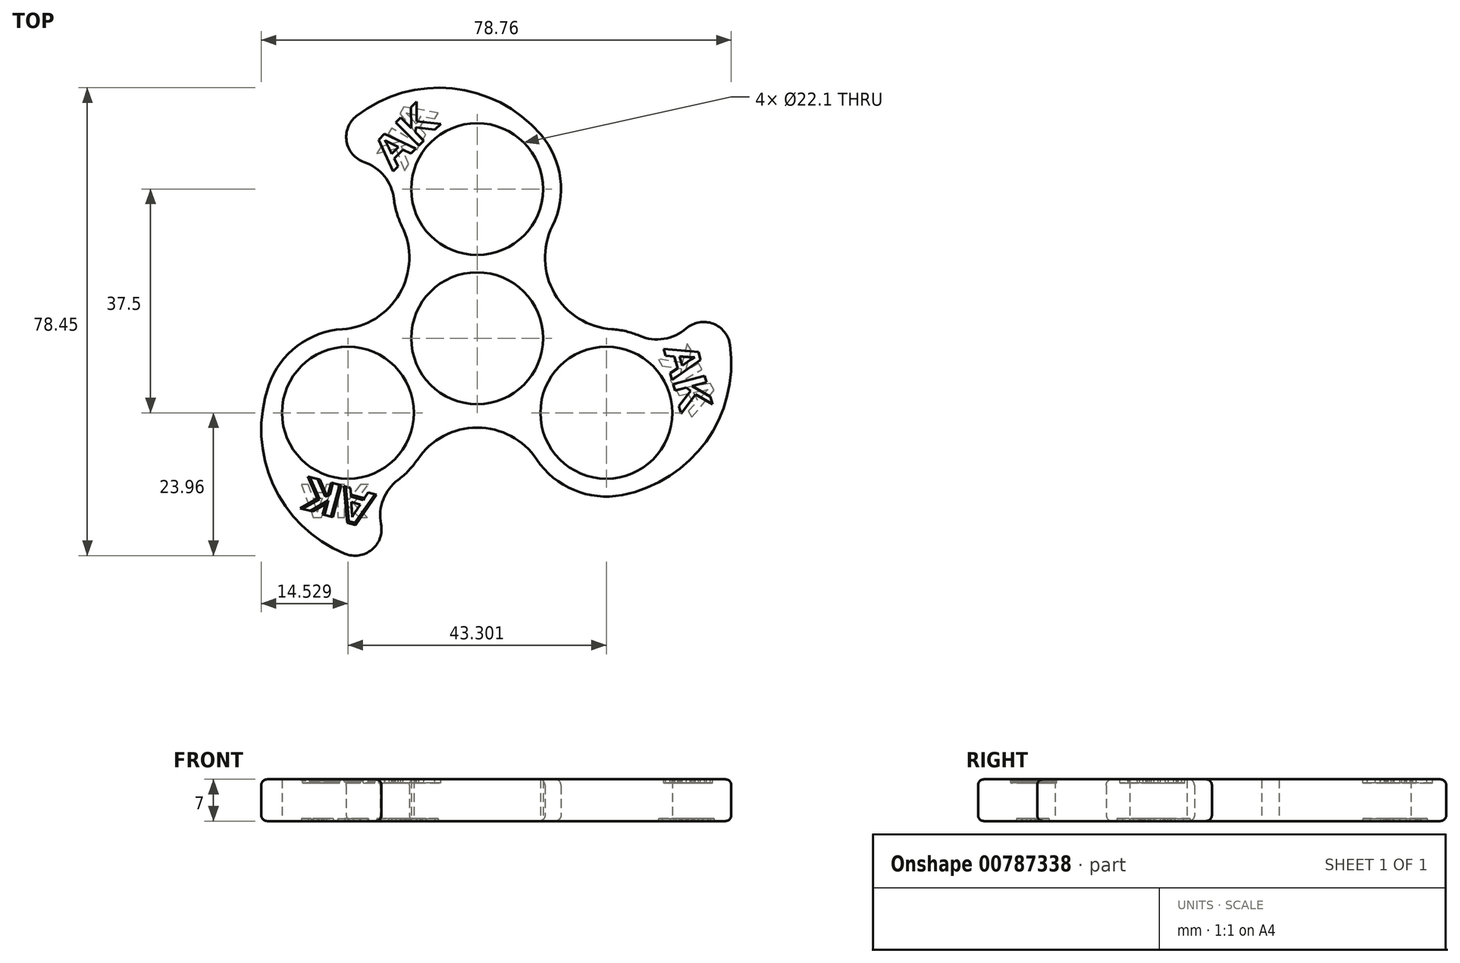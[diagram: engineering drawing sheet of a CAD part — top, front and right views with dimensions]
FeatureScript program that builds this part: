
annotation { "Feature Type Name" : "Feature", "Feature Type Description" : "" }
export const myFeature = defineFeature(function(context is Context, id is Id, definition is map)
    precondition{}
    {
        {
            var Q0;
            Q0=qCreatedBy(makeId("Top.planeOp"),FACE);
            var sketch = newSketch(context, id + "F0", { "sketchPlane" : qUnion([Q0])});
            skCircle(sketch, "E0", {"center": v(0, 0) * mm, "radius": 11.05 * mm});
            skCircle(sketch, "E1", {"center": v(0, 0) * mm, "radius": 16.5 * mm});
            skCircle(sketch, "E2", {"center": v(0, 25) * mm, "radius": 11.05 * mm});
            skCircle(sketch, "E3", {"center": v(0, 25) * mm, "radius": 14.05 * mm});
            skLineSegment(sketch, "E4", {"start": v(0, 0) * mm, "end": v(-33.5, -19.34) * mm, "construction": true});
            skLineSegment(sketch, "E5", {"start": v(35.5, -20.5) * mm, "end": v(0, 0) * mm, "construction": true});
            skLineSegment(sketch, "E6", {"start": v(0, 0) * mm, "end": v(54.09, 31.23) * mm, "construction": true});
            skCircle(sketch, "E7", {"center": v(23.37, 13.5) * mm, "radius": 12 * mm});
            skCircle(sketch, "E8", {"center": v(0, 0) * mm, "radius": 38 * mm});
            skCircle(sketch, "E9.1.0", {"center": v(-23.37, 13.5) * mm, "radius": 12 * mm});
            skCircle(sketch, "E9.2.0", {"center": v(0, -26.99) * mm, "radius": 12 * mm});
            skCircle(sketch, "E10.1.0", {"center": v(-21.65, -12.5) * mm, "radius": 14.05 * mm});
            skCircle(sketch, "E10.1.1", {"center": v(-21.65, -12.5) * mm, "radius": 11.05 * mm});
            skCircle(sketch, "E10.2.0", {"center": v(21.65, -12.5) * mm, "radius": 14.05 * mm});
            skCircle(sketch, "E10.2.1", {"center": v(21.65, -12.5) * mm, "radius": 11.05 * mm});
            skCircle(sketch, "E11", {"center": v(-17.48, 33.74) * mm, "radius": 4.46 * mm});
            skCircle(sketch, "E12", {"center": v(-21.34, 22.5) * mm, "radius": 7.43 * mm});
            skCircle(sketch, "E13", {"center": v(-6.4, 19.5) * mm, "radius": 22.5 * mm});
            skCircle(sketch, "E14.1.0", {"center": v(-20.48, -32) * mm, "radius": 4.46 * mm});
            skCircle(sketch, "E14.1.1", {"center": v(-13.68, -15.3) * mm, "radius": 22.5 * mm});
            skCircle(sketch, "E14.1.2", {"center": v(-8.82, -29.73) * mm, "radius": 7.43 * mm});
            skCircle(sketch, "E14.2.0", {"center": v(37.96, -1.73) * mm, "radius": 4.46 * mm});
            skCircle(sketch, "E14.2.1", {"center": v(20.08, -4.2) * mm, "radius": 22.5 * mm});
            skCircle(sketch, "E14.2.2", {"center": v(30.15, 7.23) * mm, "radius": 7.43 * mm});
            skSolve(sketch);
        }
        {
            var Q0;
            {var subQ0=sQuery(id+"F0.wireOp",EDGE,"E8");var subQ1=sQuery(id+"F0.wireOp",EDGE,"E3");var subQ2=makeQuery(id+"F0.imprint","INTERSECT",VERTEX,{"disambiguationData":[OD(0.0)],"derivedFrom":[subQ1,subQ0]});Q0=makeQuery(id+"F0.imprint","IMPRINT",FACE,{"disambiguationData":[TD([[makeQuery(id+"F0.imprint","IMPRINT",EDGE,{"disambiguationData":[TD([[subQ2,-1.0]])],"derivedFrom":subQ1}),1.0]])]});}
            var Q1;
            {var subQ1=sQuery(id+"F0.wireOp",EDGE,"E3");var subQ6=sQuery(id+"F0.wireOp",EDGE,"E1");var subQ11=makeQuery(id+"F0.imprint","INTERSECT",VERTEX,{"disambiguationData":[OD(0.0)],"derivedFrom":[subQ6,subQ1]});Q1=makeQuery(id+"F0.imprint","IMPRINT",FACE,{"disambiguationData":[TD([[makeQuery(id+"F0.imprint","IMPRINT",EDGE,{"disambiguationData":[TD([[subQ11,-1.0]])],"derivedFrom":subQ6}),-1.0]])]});}
            var Q2;
            {var subQ0=sQuery(id+"F0.wireOp",EDGE,"E9.1.0");var subQ1=sQuery(id+"F0.wireOp",EDGE,"E3");var subQ2=makeQuery(id+"F0.imprint","INTERSECT",VERTEX,{"disambiguationData":[OD(0.0)],"derivedFrom":[subQ1,subQ0]});Q2=makeQuery(id+"F0.imprint","IMPRINT",FACE,{"disambiguationData":[TD([[makeQuery(id+"F0.imprint","IMPRINT",EDGE,{"disambiguationData":[TD([[subQ2,-1.0]])],"derivedFrom":subQ1}),1.0]])]});}
            var Q3;
            {var subQ0=sQuery(id+"F0.wireOp",EDGE,"E7");var subQ1=sQuery(id+"F0.wireOp",EDGE,"E3");var subQ2=makeQuery(id+"F0.imprint","INTERSECT",VERTEX,{"disambiguationData":[OD(0.0)],"derivedFrom":[subQ1,subQ0]});Q3=makeQuery(id+"F0.imprint","IMPRINT",FACE,{"disambiguationData":[TD([[makeQuery(id+"F0.imprint","IMPRINT",EDGE,{"disambiguationData":[TD([[subQ2,1.0]])],"derivedFrom":subQ1}),1.0]])]});}
            var Q4;
            {var subQ4=sQuery(id+"F0.wireOp",EDGE,"E3");var subQ7=sQuery(id+"F0.wireOp",EDGE,"E0");var subQ8=makeQuery(id+"F0.imprint","INTERSECT",VERTEX,{"disambiguationData":[OD(0.0)],"derivedFrom":[subQ7,subQ4]});Q4=makeQuery(id+"F0.imprint","IMPRINT",FACE,{"disambiguationData":[TD([[makeQuery(id+"F0.imprint","IMPRINT",EDGE,{"disambiguationData":[TD([[subQ8,-1.0]])],"derivedFrom":subQ7}),-1.0]])]});}
            var Q5;
            {var subQ0=sQuery(id+"F0.wireOp",EDGE,"E3");var subQ1=sQuery(id+"F0.wireOp",EDGE,"E0");var subQ2=makeQuery(id+"F0.imprint","INTERSECT",VERTEX,{"disambiguationData":[OD(1.0)],"derivedFrom":[subQ1,subQ0]});Q5=makeQuery(id+"F0.imprint","IMPRINT",FACE,{"disambiguationData":[TD([[makeQuery(id+"F0.imprint","IMPRINT",EDGE,{"disambiguationData":[TD([[subQ2,-1.0]])],"derivedFrom":subQ1}),-1.0]])]});}
            var Q6;
            {var subQ0=sQuery(id+"F0.wireOp",EDGE,"E3");var subQ1=sQuery(id+"F0.wireOp",EDGE,"E0");var subQ2=makeQuery(id+"F0.imprint","INTERSECT",VERTEX,{"disambiguationData":[OD(0.0)],"derivedFrom":[subQ1,subQ0]});Q6=makeQuery(id+"F0.imprint","IMPRINT",FACE,{"disambiguationData":[TD([[makeQuery(id+"F0.imprint","IMPRINT",EDGE,{"disambiguationData":[TD([[subQ2,1.0]])],"derivedFrom":subQ1}),-1.0]])]});}
            var Q7;
            {var subQ0=sQuery(id+"F0.wireOp",EDGE,"E10.2.0");var subQ1=sQuery(id+"F0.wireOp",EDGE,"E0");var subQ2=makeQuery(id+"F0.imprint","INTERSECT",VERTEX,{"disambiguationData":[OD(0.0)],"derivedFrom":[subQ1,subQ0]});Q7=makeQuery(id+"F0.imprint","IMPRINT",FACE,{"disambiguationData":[TD([[makeQuery(id+"F0.imprint","IMPRINT",EDGE,{"disambiguationData":[TD([[subQ2,1.0]])],"derivedFrom":subQ1}),-1.0]])]});}
            var Q8;
            {var subQ0=sQuery(id+"F0.wireOp",EDGE,"E10.1.0");var subQ1=sQuery(id+"F0.wireOp",EDGE,"E0");var subQ2=makeQuery(id+"F0.imprint","INTERSECT",VERTEX,{"disambiguationData":[OD(1.0)],"derivedFrom":[subQ1,subQ0]});Q8=makeQuery(id+"F0.imprint","IMPRINT",FACE,{"disambiguationData":[TD([[makeQuery(id+"F0.imprint","IMPRINT",EDGE,{"disambiguationData":[TD([[subQ2,-1.0]])],"derivedFrom":subQ1}),-1.0]])]});}
            var Q9;
            {var subQ0=sQuery(id+"F0.wireOp",EDGE,"E10.1.0");var subQ1=sQuery(id+"F0.wireOp",EDGE,"E0");var subQ9=makeQuery(id+"F0.imprint","INTERSECT",VERTEX,{"disambiguationData":[OD(0.0)],"derivedFrom":[subQ1,subQ0]});Q9=makeQuery(id+"F0.imprint","IMPRINT",FACE,{"disambiguationData":[TD([[makeQuery(id+"F0.imprint","IMPRINT",EDGE,{"disambiguationData":[TD([[subQ9,-1.0]])],"derivedFrom":subQ1}),-1.0]])]});}
            var Q10;
            {var subQ0=sQuery(id+"F0.wireOp",EDGE,"E10.1.0");var subQ7=sQuery(id+"F0.wireOp",EDGE,"E1");var subQ14=makeQuery(id+"F0.imprint","INTERSECT",VERTEX,{"disambiguationData":[OD(0.0)],"derivedFrom":[subQ7,subQ0]});Q10=makeQuery(id+"F0.imprint","IMPRINT",FACE,{"disambiguationData":[TD([[makeQuery(id+"F0.imprint","IMPRINT",EDGE,{"disambiguationData":[TD([[subQ14,-1.0]])],"derivedFrom":subQ7}),-1.0]])]});}
            var Q11;
            {var subQ0=sQuery(id+"F0.wireOp",EDGE,"E10.1.0");var subQ1=sQuery(id+"F0.wireOp",EDGE,"E8");var subQ2=makeQuery(id+"F0.imprint","INTERSECT",VERTEX,{"disambiguationData":[OD(0.0)],"derivedFrom":[subQ1,subQ0]});Q11=makeQuery(id+"F0.imprint","IMPRINT",FACE,{"disambiguationData":[TD([[makeQuery(id+"F0.imprint","IMPRINT",EDGE,{"disambiguationData":[TD([[subQ2,-1.0]])],"derivedFrom":subQ1}),-1.0]])]});}
            var Q12;
            {var subQ0=sQuery(id+"F0.wireOp",EDGE,"E10.2.0");var subQ7=sQuery(id+"F0.wireOp",EDGE,"E1");var subQ15=makeQuery(id+"F0.imprint","INTERSECT",VERTEX,{"disambiguationData":[OD(1.0)],"derivedFrom":[subQ7,subQ0]});Q12=makeQuery(id+"F0.imprint","IMPRINT",FACE,{"disambiguationData":[TD([[makeQuery(id+"F0.imprint","IMPRINT",EDGE,{"disambiguationData":[TD([[subQ15,-1.0]])],"derivedFrom":subQ7}),-1.0]])]});}
            var Q13;
            {var subQ0=sQuery(id+"F0.wireOp",EDGE,"E10.2.0");var subQ1=sQuery(id+"F0.wireOp",EDGE,"E8");var subQ2=makeQuery(id+"F0.imprint","INTERSECT",VERTEX,{"disambiguationData":[OD(0.0)],"derivedFrom":[subQ1,subQ0]});Q13=makeQuery(id+"F0.imprint","IMPRINT",FACE,{"disambiguationData":[TD([[makeQuery(id+"F0.imprint","IMPRINT",EDGE,{"disambiguationData":[TD([[subQ2,-1.0]])],"derivedFrom":subQ1}),-1.0]])]});}
            var Q14;
            {var subQ0=sQuery(id+"F0.wireOp",EDGE,"E3");var subQ1=sQuery(id+"F0.wireOp",EDGE,"E1");var subQ2=makeQuery(id+"F0.imprint","INTERSECT",VERTEX,{"disambiguationData":[OD(0.0)],"derivedFrom":[subQ1,subQ0]});Q14=makeQuery(id+"F0.imprint","IMPRINT",FACE,{"disambiguationData":[TD([[makeQuery(id+"F0.imprint","IMPRINT",EDGE,{"disambiguationData":[TD([[subQ2,1.0]])],"derivedFrom":subQ1}),-1.0]])]});}
            var Q15;
            {var subQ0=sQuery(id+"F0.wireOp",EDGE,"E3");var subQ1=sQuery(id+"F0.wireOp",EDGE,"E1");var subQ2=makeQuery(id+"F0.imprint","INTERSECT",VERTEX,{"disambiguationData":[OD(1.0)],"derivedFrom":[subQ1,subQ0]});Q15=makeQuery(id+"F0.imprint","IMPRINT",FACE,{"disambiguationData":[TD([[makeQuery(id+"F0.imprint","IMPRINT",EDGE,{"disambiguationData":[TD([[subQ2,-1.0]])],"derivedFrom":subQ1}),-1.0]])]});}
            var Q16;
            {var subQ0=sQuery(id+"F0.wireOp",EDGE,"E10.1.0");var subQ1=sQuery(id+"F0.wireOp",EDGE,"E1");var subQ2=makeQuery(id+"F0.imprint","INTERSECT",VERTEX,{"disambiguationData":[OD(1.0)],"derivedFrom":[subQ1,subQ0]});Q16=makeQuery(id+"F0.imprint","IMPRINT",FACE,{"disambiguationData":[TD([[makeQuery(id+"F0.imprint","IMPRINT",EDGE,{"disambiguationData":[TD([[subQ2,-1.0]])],"derivedFrom":subQ1}),-1.0]])]});}
            var Q17;
            {var subQ0=sQuery(id+"F0.wireOp",EDGE,"E8");var subQ1=sQuery(id+"F0.wireOp",EDGE,"E3");var subQ2=makeQuery(id+"F0.imprint","INTERSECT",VERTEX,{"disambiguationData":[OD(0.0)],"derivedFrom":[subQ1,subQ0]});Q17=makeQuery(id+"F0.imprint","IMPRINT",FACE,{"disambiguationData":[TD([[makeQuery(id+"F0.imprint","IMPRINT",EDGE,{"disambiguationData":[TD([[subQ2,1.0]])],"derivedFrom":subQ1}),1.0]])]});}
            var Q18;
            {var subQ0=sQuery(id+"F0.wireOp",EDGE,"E10.1.0");var subQ2=sQuery(id+"F0.wireOp",EDGE,"E1");var subQ4=makeQuery(id+"F0.imprint","INTERSECT",VERTEX,{"disambiguationData":[OD(0.0)],"derivedFrom":[subQ2,subQ0]});Q18=makeQuery(id+"F0.imprint","IMPRINT",FACE,{"disambiguationData":[TD([[makeQuery(id+"F0.imprint","IMPRINT",EDGE,{"disambiguationData":[TD([[subQ4,-1.0]])],"derivedFrom":subQ2}),1.0]])]});}
            var Q19;
            {var subQ1=sQuery(id+"F0.wireOp",EDGE,"E1");var subQ3=sQuery(id+"F0.wireOp",EDGE,"E3");var subQ7=makeQuery(id+"F0.imprint","INTERSECT",VERTEX,{"disambiguationData":[OD(0.0)],"derivedFrom":[subQ1,subQ3]});Q19=makeQuery(id+"F0.imprint","IMPRINT",FACE,{"disambiguationData":[TD([[makeQuery(id+"F0.imprint","IMPRINT",EDGE,{"disambiguationData":[TD([[subQ7,-1.0]])],"derivedFrom":subQ1}),1.0]])]});}
            var Q20;
            {var subQ0=sQuery(id+"F0.wireOp",EDGE,"E10.2.0");var subQ2=sQuery(id+"F0.wireOp",EDGE,"E1");var subQ6=makeQuery(id+"F0.imprint","INTERSECT",VERTEX,{"disambiguationData":[OD(1.0)],"derivedFrom":[subQ2,subQ0]});Q20=makeQuery(id+"F0.imprint","IMPRINT",FACE,{"disambiguationData":[TD([[makeQuery(id+"F0.imprint","IMPRINT",EDGE,{"disambiguationData":[TD([[subQ6,-1.0]])],"derivedFrom":subQ2}),1.0]])]});}
            var Q21;
            {var subQ0=sQuery(id+"F0.wireOp",EDGE,"E7");var subQ1=sQuery(id+"F0.wireOp",EDGE,"E1");var subQ2=makeQuery(id+"F0.imprint","INTERSECT",VERTEX,{"disambiguationData":[OD(0.0)],"derivedFrom":[subQ1,subQ0]});Q21=makeQuery(id+"F0.imprint","IMPRINT",FACE,{"disambiguationData":[TD([[makeQuery(id+"F0.imprint","IMPRINT",EDGE,{"disambiguationData":[TD([[subQ2,1.0]])],"derivedFrom":subQ1}),-1.0]])]});}
            var Q22;
            {var subQ0=sQuery(id+"F0.wireOp",EDGE,"E9.1.0");var subQ1=sQuery(id+"F0.wireOp",EDGE,"E1");var subQ2=makeQuery(id+"F0.imprint","INTERSECT",VERTEX,{"disambiguationData":[OD(1.0)],"derivedFrom":[subQ1,subQ0]});Q22=makeQuery(id+"F0.imprint","IMPRINT",FACE,{"disambiguationData":[TD([[makeQuery(id+"F0.imprint","IMPRINT",EDGE,{"disambiguationData":[TD([[subQ2,-1.0]])],"derivedFrom":subQ1}),-1.0]])]});}
            var Q23;
            {var subQ0=sQuery(id+"F0.wireOp",EDGE,"E9.2.0");var subQ1=sQuery(id+"F0.wireOp",EDGE,"E1");var subQ2=makeQuery(id+"F0.imprint","INTERSECT",VERTEX,{"disambiguationData":[OD(1.0)],"derivedFrom":[subQ1,subQ0]});Q23=makeQuery(id+"F0.imprint","IMPRINT",FACE,{"disambiguationData":[TD([[makeQuery(id+"F0.imprint","IMPRINT",EDGE,{"disambiguationData":[TD([[subQ2,-1.0]])],"derivedFrom":subQ1}),-1.0]])]});}
            var Q24;
            {var subQ0=sQuery(id+"F0.wireOp",EDGE,"E8");var subQ1=sQuery(id+"F0.wireOp",EDGE,"E3");var subQ2=makeQuery(id+"F0.imprint","INTERSECT",VERTEX,{"disambiguationData":[OD(1.0)],"derivedFrom":[subQ1,subQ0]});Q24=makeQuery(id+"F0.imprint","IMPRINT",FACE,{"disambiguationData":[TD([[makeQuery(id+"F0.imprint","IMPRINT",EDGE,{"disambiguationData":[TD([[subQ2,-1.0]])],"derivedFrom":subQ1}),-1.0]])]});}
            var Q25;
            {var subQ0=sQuery(id+"F0.wireOp",EDGE,"E8");var subQ1=sQuery(id+"F0.wireOp",EDGE,"E3");var subQ2=makeQuery(id+"F0.imprint","INTERSECT",VERTEX,{"disambiguationData":[OD(0.0)],"derivedFrom":[subQ1,subQ0]});Q25=makeQuery(id+"F0.imprint","IMPRINT",FACE,{"disambiguationData":[TD([[makeQuery(id+"F0.imprint","IMPRINT",EDGE,{"disambiguationData":[TD([[subQ2,-1.0]])],"derivedFrom":subQ1}),-1.0]])]});}
            var Q26;
            {var subQ0=sQuery(id+"F0.wireOp",EDGE,"E11");var subQ1=sQuery(id+"F0.wireOp",EDGE,"E8");var subQ2=makeQuery(id+"F0.imprint","INTERSECT",VERTEX,{"disambiguationData":[OD(0.0)],"derivedFrom":[subQ1,subQ0]});Q26=makeQuery(id+"F0.imprint","IMPRINT",FACE,{"disambiguationData":[TD([[makeQuery(id+"F0.imprint","IMPRINT",EDGE,{"disambiguationData":[TD([[subQ2,-1.0]])],"derivedFrom":subQ1}),1.0]])]});}
            var Q27;
            {var subQ2=sQuery(id+"F0.wireOp",EDGE,"E13");var subQ4=sQuery(id+"F0.wireOp",EDGE,"E1");var subQ5=makeQuery(id+"F0.imprint","INTERSECT",VERTEX,{"disambiguationData":[OD(1.0)],"derivedFrom":[subQ4,subQ2]});Q27=makeQuery(id+"F0.imprint","IMPRINT",FACE,{"disambiguationData":[TD([[makeQuery(id+"F0.imprint","IMPRINT",EDGE,{"disambiguationData":[TD([[subQ5,-1.0]])],"derivedFrom":subQ4}),1.0]])]});}
            var Q28;
            {var subQ0=sQuery(id+"F0.wireOp",EDGE,"E13");var subQ1=sQuery(id+"F0.wireOp",EDGE,"E0");var subQ2=makeQuery(id+"F0.imprint","INTERSECT",VERTEX,{"disambiguationData":[OD(1.0)],"derivedFrom":[subQ1,subQ0]});Q28=makeQuery(id+"F0.imprint","IMPRINT",FACE,{"disambiguationData":[TD([[makeQuery(id+"F0.imprint","IMPRINT",EDGE,{"disambiguationData":[TD([[subQ2,-1.0]])],"derivedFrom":subQ1}),-1.0]])]});}
            var Q29;
            {var subQ0=sQuery(id+"F0.wireOp",EDGE,"E11");var subQ1=sQuery(id+"F0.wireOp",EDGE,"E8");var subQ2=makeQuery(id+"F0.imprint","INTERSECT",VERTEX,{"disambiguationData":[OD(0.0)],"derivedFrom":[subQ1,subQ0]});Q29=makeQuery(id+"F0.imprint","IMPRINT",FACE,{"disambiguationData":[TD([[makeQuery(id+"F0.imprint","IMPRINT",EDGE,{"disambiguationData":[TD([[subQ2,-1.0]])],"derivedFrom":subQ1}),-1.0]])]});}
            var Q30;
            {var subQ2=sQuery(id+"F0.wireOp",EDGE,"E1");var subQ7=sQuery(id+"F0.wireOp",EDGE,"E14.2.1");var subQ8=makeQuery(id+"F0.imprint","INTERSECT",VERTEX,{"disambiguationData":[OD(0.0)],"derivedFrom":[subQ2,subQ7]});Q30=makeQuery(id+"F0.imprint","IMPRINT",FACE,{"disambiguationData":[TD([[makeQuery(id+"F0.imprint","IMPRINT",EDGE,{"disambiguationData":[TD([[subQ8,-1.0]])],"derivedFrom":subQ2}),1.0]])]});}
            var Q31;
            {var subQ7=sQuery(id+"F0.wireOp",EDGE,"E14.2.1");var subQ9=sQuery(id+"F0.wireOp",EDGE,"E0");var subQ10=makeQuery(id+"F0.imprint","INTERSECT",VERTEX,{"disambiguationData":[OD(0.0)],"derivedFrom":[subQ9,subQ7]});Q31=makeQuery(id+"F0.imprint","IMPRINT",FACE,{"disambiguationData":[TD([[makeQuery(id+"F0.imprint","IMPRINT",EDGE,{"disambiguationData":[TD([[subQ10,1.0]])],"derivedFrom":subQ9}),-1.0]])]});}
            var Q32;
            {var subQ0=sQuery(id+"F0.wireOp",EDGE,"E14.2.1");var subQ1=sQuery(id+"F0.wireOp",EDGE,"E3");var subQ2=makeQuery(id+"F0.imprint","INTERSECT",VERTEX,{"disambiguationData":[OD(1.0)],"derivedFrom":[subQ1,subQ0]});Q32=makeQuery(id+"F0.imprint","IMPRINT",FACE,{"disambiguationData":[TD([[makeQuery(id+"F0.imprint","IMPRINT",EDGE,{"disambiguationData":[TD([[subQ2,-1.0]])],"derivedFrom":subQ1}),-1.0]])]});}
            var Q33;
            {var subQ1=sQuery(id+"F0.wireOp",EDGE,"E0");var subQ7=sQuery(id+"F0.wireOp",EDGE,"E13");var subQ9=makeQuery(id+"F0.imprint","INTERSECT",VERTEX,{"disambiguationData":[OD(0.0)],"derivedFrom":[subQ1,subQ7]});Q33=makeQuery(id+"F0.imprint","IMPRINT",FACE,{"disambiguationData":[TD([[makeQuery(id+"F0.imprint","IMPRINT",EDGE,{"disambiguationData":[TD([[subQ9,1.0]])],"derivedFrom":subQ1}),-1.0]])]});}
            var Q34;
            {var subQ2=sQuery(id+"F0.wireOp",EDGE,"E14.1.1");var subQ4=sQuery(id+"F0.wireOp",EDGE,"E1");var subQ8=makeQuery(id+"F0.imprint","INTERSECT",VERTEX,{"disambiguationData":[OD(1.0)],"derivedFrom":[subQ4,subQ2]});Q34=makeQuery(id+"F0.imprint","IMPRINT",FACE,{"disambiguationData":[TD([[makeQuery(id+"F0.imprint","IMPRINT",EDGE,{"disambiguationData":[TD([[subQ8,-1.0]])],"derivedFrom":subQ4}),1.0]])]});}
            var Q35;
            {var subQ0=sQuery(id+"F0.wireOp",EDGE,"E10.2.0");var subQ1=sQuery(id+"F0.wireOp",EDGE,"E9.2.0");var subQ2=makeQuery(id+"F0.imprint","INTERSECT",VERTEX,{"derivedFrom":[subQ1,subQ0]});Q35=makeQuery(id+"F0.imprint","IMPRINT",FACE,{"disambiguationData":[TD([[makeQuery(id+"F0.imprint","IMPRINT",EDGE,{"disambiguationData":[TD([[subQ2,-1.0]])],"derivedFrom":subQ1}),-1.0]])]});}
            var Q36;
            {var subQ1=sQuery(id+"F0.wireOp",EDGE,"E1");var subQ7=sQuery(id+"F0.wireOp",EDGE,"E14.1.1");var subQ14=makeQuery(id+"F0.imprint","INTERSECT",VERTEX,{"disambiguationData":[OD(1.0)],"derivedFrom":[subQ1,subQ7]});Q36=makeQuery(id+"F0.imprint","IMPRINT",FACE,{"disambiguationData":[TD([[makeQuery(id+"F0.imprint","IMPRINT",EDGE,{"disambiguationData":[TD([[subQ14,-1.0]])],"derivedFrom":subQ1}),-1.0]])]});}
            var Q37;
            {var subQ7=sQuery(id+"F0.wireOp",EDGE,"E14.2.1");var subQ9=sQuery(id+"F0.wireOp",EDGE,"E0");var subQ10=makeQuery(id+"F0.imprint","INTERSECT",VERTEX,{"disambiguationData":[OD(1.0)],"derivedFrom":[subQ9,subQ7]});Q37=makeQuery(id+"F0.imprint","IMPRINT",FACE,{"disambiguationData":[TD([[makeQuery(id+"F0.imprint","IMPRINT",EDGE,{"disambiguationData":[TD([[subQ10,-1.0]])],"derivedFrom":subQ9}),-1.0]])]});}
            var Q38;
            {var subQ7=sQuery(id+"F0.wireOp",EDGE,"E14.1.1");var subQ9=sQuery(id+"F0.wireOp",EDGE,"E0");var subQ10=makeQuery(id+"F0.imprint","INTERSECT",VERTEX,{"disambiguationData":[OD(0.0)],"derivedFrom":[subQ9,subQ7]});Q38=makeQuery(id+"F0.imprint","IMPRINT",FACE,{"disambiguationData":[TD([[makeQuery(id+"F0.imprint","IMPRINT",EDGE,{"disambiguationData":[TD([[subQ10,-1.0]])],"derivedFrom":subQ9}),-1.0]])]});}
            var Q39;
            {var subQ1=sQuery(id+"F0.wireOp",EDGE,"E1");var subQ12=sQuery(id+"F0.wireOp",EDGE,"E13");var subQ13=makeQuery(id+"F0.imprint","INTERSECT",VERTEX,{"disambiguationData":[OD(1.0)],"derivedFrom":[subQ1,subQ12]});Q39=makeQuery(id+"F0.imprint","IMPRINT",FACE,{"disambiguationData":[TD([[makeQuery(id+"F0.imprint","IMPRINT",EDGE,{"disambiguationData":[TD([[subQ13,-1.0]])],"derivedFrom":subQ1}),-1.0]])]});}
            var Q40;
            {var subQ0=sQuery(id+"F0.wireOp",EDGE,"E10.1.0");var subQ1=sQuery(id+"F0.wireOp",EDGE,"E9.1.0");var subQ2=makeQuery(id+"F0.imprint","INTERSECT",VERTEX,{"derivedFrom":[subQ1,subQ0]});Q40=makeQuery(id+"F0.imprint","IMPRINT",FACE,{"disambiguationData":[TD([[makeQuery(id+"F0.imprint","IMPRINT",EDGE,{"disambiguationData":[TD([[subQ2,-1.0]])],"derivedFrom":subQ1}),-1.0]])]});}
            var Q41;
            {var subQ0=sQuery(id+"F0.wireOp",EDGE,"E14.2.0");var subQ1=sQuery(id+"F0.wireOp",EDGE,"E8");var subQ2=makeQuery(id+"F0.imprint","INTERSECT",VERTEX,{"disambiguationData":[OD(0.0)],"derivedFrom":[subQ1,subQ0]});Q41=makeQuery(id+"F0.imprint","IMPRINT",FACE,{"disambiguationData":[TD([[makeQuery(id+"F0.imprint","IMPRINT",EDGE,{"disambiguationData":[TD([[subQ2,1.0]])],"derivedFrom":subQ1}),-1.0]])]});}
            var Q42;
            {var subQ0=sQuery(id+"F0.wireOp",EDGE,"E14.2.0");var subQ1=sQuery(id+"F0.wireOp",EDGE,"E8");var subQ2=makeQuery(id+"F0.imprint","INTERSECT",VERTEX,{"disambiguationData":[OD(0.0)],"derivedFrom":[subQ1,subQ0]});Q42=makeQuery(id+"F0.imprint","IMPRINT",FACE,{"disambiguationData":[TD([[makeQuery(id+"F0.imprint","IMPRINT",EDGE,{"disambiguationData":[TD([[subQ2,1.0]])],"derivedFrom":subQ1}),1.0]])]});}
            var Q43;
            {var subQ0=sQuery(id+"F0.wireOp",EDGE,"E10.2.0");var subQ1=sQuery(id+"F0.wireOp",EDGE,"E8");var subQ2=makeQuery(id+"F0.imprint","INTERSECT",VERTEX,{"disambiguationData":[OD(1.0)],"derivedFrom":[subQ1,subQ0]});Q43=makeQuery(id+"F0.imprint","IMPRINT",FACE,{"disambiguationData":[TD([[makeQuery(id+"F0.imprint","IMPRINT",EDGE,{"disambiguationData":[TD([[subQ2,-1.0]])],"derivedFrom":subQ1}),1.0]])]});}
            var Q44;
            {var subQ0=sQuery(id+"F0.wireOp",EDGE,"E10.1.0");var subQ1=sQuery(id+"F0.wireOp",EDGE,"E8");var subQ2=makeQuery(id+"F0.imprint","INTERSECT",VERTEX,{"disambiguationData":[OD(1.0)],"derivedFrom":[subQ1,subQ0]});Q44=makeQuery(id+"F0.imprint","IMPRINT",FACE,{"disambiguationData":[TD([[makeQuery(id+"F0.imprint","IMPRINT",EDGE,{"disambiguationData":[TD([[subQ2,-1.0]])],"derivedFrom":subQ1}),1.0]])]});}
            var Q45;
            {var subQ0=sQuery(id+"F0.wireOp",EDGE,"E14.1.0");var subQ1=sQuery(id+"F0.wireOp",EDGE,"E8");var subQ2=makeQuery(id+"F0.imprint","INTERSECT",VERTEX,{"disambiguationData":[OD(0.0)],"derivedFrom":[subQ1,subQ0]});Q45=makeQuery(id+"F0.imprint","IMPRINT",FACE,{"disambiguationData":[TD([[makeQuery(id+"F0.imprint","IMPRINT",EDGE,{"disambiguationData":[TD([[subQ2,-1.0]])],"derivedFrom":subQ1}),1.0]])]});}
            var Q46;
            {var subQ0=sQuery(id+"F0.wireOp",EDGE,"E14.1.1");var subQ3=sQuery(id+"F0.wireOp",EDGE,"E8");var subQ8=makeQuery(id+"F0.imprint","INTERSECT",VERTEX,{"disambiguationData":[OD(0.0)],"derivedFrom":[subQ3,subQ0]});Q46=makeQuery(id+"F0.imprint","IMPRINT",FACE,{"disambiguationData":[TD([[makeQuery(id+"F0.imprint","IMPRINT",EDGE,{"disambiguationData":[TD([[subQ8,-1.0]])],"derivedFrom":subQ3}),-1.0]])]});}
            var Q47;
            {var subQ0=sQuery(id+"F0.wireOp",EDGE,"E14.1.0");var subQ1=sQuery(id+"F0.wireOp",EDGE,"E8");var subQ2=makeQuery(id+"F0.imprint","INTERSECT",VERTEX,{"disambiguationData":[OD(0.0)],"derivedFrom":[subQ1,subQ0]});Q47=makeQuery(id+"F0.imprint","IMPRINT",FACE,{"disambiguationData":[TD([[makeQuery(id+"F0.imprint","IMPRINT",EDGE,{"disambiguationData":[TD([[subQ2,-1.0]])],"derivedFrom":subQ1}),-1.0]])]});}
            var Q48;
            {var subQ0=sQuery(id+"F0.wireOp",EDGE,"E8");var subQ1=sQuery(id+"F0.wireOp",EDGE,"E3");var subQ2=makeQuery(id+"F0.imprint","INTERSECT",VERTEX,{"disambiguationData":[OD(0.0)],"derivedFrom":[subQ1,subQ0]});Q48=makeQuery(id+"F0.imprint","IMPRINT",FACE,{"disambiguationData":[TD([[makeQuery(id+"F0.imprint","IMPRINT",EDGE,{"disambiguationData":[TD([[subQ2,1.0]])],"derivedFrom":subQ1}),-1.0]])]});}
            var Q49;
            {var subQ0=sQuery(id+"F0.wireOp",EDGE,"E14.1.1");var subQ1=sQuery(id+"F0.wireOp",EDGE,"E8");var subQ2=makeQuery(id+"F0.imprint","INTERSECT",VERTEX,{"disambiguationData":[OD(0.0)],"derivedFrom":[subQ1,subQ0]});Q49=makeQuery(id+"F0.imprint","IMPRINT",FACE,{"disambiguationData":[TD([[makeQuery(id+"F0.imprint","IMPRINT",EDGE,{"disambiguationData":[TD([[subQ2,-1.0]])],"derivedFrom":subQ1}),1.0]])]});}
            var Q50;
            {var subQ1=sQuery(id+"F0.wireOp",EDGE,"E8");var subQ4=sQuery(id+"F0.wireOp",EDGE,"E14.2.1");var subQ8=makeQuery(id+"F0.imprint","INTERSECT",VERTEX,{"disambiguationData":[OD(0.0)],"derivedFrom":[subQ1,subQ4]});Q50=makeQuery(id+"F0.imprint","IMPRINT",FACE,{"disambiguationData":[TD([[makeQuery(id+"F0.imprint","IMPRINT",EDGE,{"disambiguationData":[TD([[subQ8,-1.0]])],"derivedFrom":subQ1}),-1.0]])]});}
            var Q51;
            {var subQ0=sQuery(id+"F0.wireOp",EDGE,"E14.2.1");var subQ1=sQuery(id+"F0.wireOp",EDGE,"E8");var subQ2=makeQuery(id+"F0.imprint","INTERSECT",VERTEX,{"disambiguationData":[OD(0.0)],"derivedFrom":[subQ1,subQ0]});Q51=makeQuery(id+"F0.imprint","IMPRINT",FACE,{"disambiguationData":[TD([[makeQuery(id+"F0.imprint","IMPRINT",EDGE,{"disambiguationData":[TD([[subQ2,-1.0]])],"derivedFrom":subQ1}),1.0]])]});}
            extrude(context, id + "F1", {"entities" : qUnion([Q0, Q1, Q2, Q3, Q4, Q5, Q6, Q7, Q8, Q9, Q10, Q11, Q12, Q13, Q14, Q15, Q16, Q17, Q18, Q19, Q20, Q21, Q22, Q23, Q24, Q25, Q26, Q27, Q28, Q29, Q30, Q31, Q32, Q33, Q34, Q35, Q36, Q37, Q38, Q39, Q40, Q41, Q42, Q43, Q44, Q45, Q46, Q47, Q48, Q49, Q50, Q51]), "endBound" : BoundingType.SYMMETRIC, "depth" : 7 * mm, "offsetDistance" : 25 * mm});
        }
        {
            var Q0;
            Q0=makeQuery(id+"F1.opExtrude","CAP_EDGE",EDGE,{"disambiguationData":[OSD([sQuery(id+"F0.wireOp",EDGE,"E13")])],"isStart":false});
            var Q1;
            Q1=makeQuery(id+"F1.opExtrude","CAP_EDGE",EDGE,{"disambiguationData":[OSD([sQuery(id+"F0.wireOp",EDGE,"E13")])],"isStart":true});
            fillet(context, id + "F2", {"entities" : qUnion([Q0, Q1]), "radius" : 1 * mm, "tangentPropagation" : true, "allowEdgeOverflow" : false});
        }
        {
            var Q0;
            Q0=makeQuery(id+"F1.opExtrude","CAP_FACE",FACE,{"disambiguationData":[OSD([sQuery(id+"F0.wireOp",EDGE,"E0"),sQuery(id+"F0.wireOp",EDGE,"E2"),sQuery(id+"F0.wireOp",EDGE,"E3"),sQuery(id+"F0.wireOp",EDGE,"E7"),sQuery(id+"F0.wireOp",EDGE,"E9.1.0"),sQuery(id+"F0.wireOp",EDGE,"E9.2.0"),sQuery(id+"F0.wireOp",EDGE,"E10.1.0"),sQuery(id+"F0.wireOp",EDGE,"E10.1.1"),sQuery(id+"F0.wireOp",EDGE,"E10.2.0"),sQuery(id+"F0.wireOp",EDGE,"E10.2.1"),sQuery(id+"F0.wireOp",EDGE,"E11"),sQuery(id+"F0.wireOp",EDGE,"E12"),sQuery(id+"F0.wireOp",EDGE,"E13"),sQuery(id+"F0.wireOp",EDGE,"E14.1.0"),sQuery(id+"F0.wireOp",EDGE,"E14.1.1"),sQuery(id+"F0.wireOp",EDGE,"E14.1.2"),sQuery(id+"F0.wireOp",EDGE,"E14.2.0"),sQuery(id+"F0.wireOp",EDGE,"E14.2.1"),sQuery(id+"F0.wireOp",EDGE,"E14.2.2")])],"isStart":false});
            var sketch = newSketch(context, id + "F3", { "sketchPlane" : qUnion([Q0])});
            skLineSegment(sketch, "E15", {"start": v(-13.99, 26.64) * mm, "end": v(-0.47, 40.16) * mm, "construction": true});
            skLineSegment(sketch, "E16", {"start": v(0, 25) * mm, "end": v(-16, 25) * mm, "construction": true});
            skLineSegment(sketch, "E17", {"start": v(21.65, -12.5) * mm, "end": v(28.87, 0) * mm, "construction": true});
            skLineSegment(sketch, "E18", {"start": v(30.06, -1.2) * mm, "end": v(35.01, -19.67) * mm, "construction": true});
            skLineSegment(sketch, "E19", {"start": v(-21.65, -12.5) * mm, "end": v(0, -50) * mm, "construction": true});
            skLineSegment(sketch, "E20", {"start": v(-34.54, -20.49) * mm, "end": v(-16.07, -25.43) * mm, "construction": true});
            skText(sketch, "E21", { "text": "AK", "fontName": "Arimo-Bold.ttf"});
            skText(sketch, "E22", { "text": "AK", "fontName": "Arimo-Bold.ttf"});
            skText(sketch, "E23", { "text": "AK", "fontName": "Arimo-Bold.ttf"});
            const initialGuessF3  = {"E21": [-0.0142, 0.02785, 0.7071, 0.7071, 0.00574], "E22": [0.03121, -0.00163, 0.25882, -0.96593, 0.00574], "E23": [-0.01697, -0.02623, -0.96593, 0.25882, 0.00574]};
            skSetInitialGuess(sketch, initialGuessF3);
            skSolve(sketch);
        }
        {
            var Q0;
            Q0=makeQuery(id+"F1.opExtrude","CAP_FACE",FACE,{"disambiguationData":[OSD([sQuery(id+"F0.wireOp",EDGE,"E0"),sQuery(id+"F0.wireOp",EDGE,"E2"),sQuery(id+"F0.wireOp",EDGE,"E3"),sQuery(id+"F0.wireOp",EDGE,"E7"),sQuery(id+"F0.wireOp",EDGE,"E9.1.0"),sQuery(id+"F0.wireOp",EDGE,"E9.2.0"),sQuery(id+"F0.wireOp",EDGE,"E10.1.0"),sQuery(id+"F0.wireOp",EDGE,"E10.1.1"),sQuery(id+"F0.wireOp",EDGE,"E10.2.0"),sQuery(id+"F0.wireOp",EDGE,"E10.2.1"),sQuery(id+"F0.wireOp",EDGE,"E11"),sQuery(id+"F0.wireOp",EDGE,"E12"),sQuery(id+"F0.wireOp",EDGE,"E13"),sQuery(id+"F0.wireOp",EDGE,"E14.1.0"),sQuery(id+"F0.wireOp",EDGE,"E14.1.1"),sQuery(id+"F0.wireOp",EDGE,"E14.1.2"),sQuery(id+"F0.wireOp",EDGE,"E14.2.0"),sQuery(id+"F0.wireOp",EDGE,"E14.2.1"),sQuery(id+"F0.wireOp",EDGE,"E14.2.2")])],"isStart":true});
            var sketch = newSketch(context, id + "F4", { "sketchPlane" : qUnion([Q0])});
            skLineSegment(sketch, "E24", {"start": v(-29.06, 23.55) * mm, "end": v(-10.6, 23.55) * mm, "construction": true});
            skLineSegment(sketch, "E25", {"start": v(21.65, 12.5) * mm, "end": v(30.87, -21.91) * mm, "construction": true});
            skLineSegment(sketch, "E26", {"start": v(35.48, 14.35) * mm, "end": v(25.7, -2.6) * mm, "construction": true});
            skLineSegment(sketch, "E27", {"start": v(0, -25) * mm, "end": v(-93.3, 0) * mm, "construction": true});
            skLineSegment(sketch, "E28", {"start": v(-15.1, -20.96) * mm, "end": v(-2.46, -42.84) * mm, "construction": true});
            skText(sketch, "E29", { "text": "AK", "fontName": "Arimo-Bold.ttf"});
            skText(sketch, "E30", { "text": "AK", "fontName": "Arimo-Bold.ttf"});
            skText(sketch, "E31", { "text": "AK", "fontName": "Arimo-Bold.ttf"});
            skLineSegment(sketch, "E32", {"start": v(-21.65, 12.5) * mm, "end": v(0, 34.15) * mm, "construction": true});
            const initialGuessF4  = {"E29": [-0.02965, 0.02455, 1, 0, 0.00574], "E30": [0.03608, 0.0134, -0.5, -0.86603, 0.00574], "E31": [-0.00644, -0.03795, -0.5, 0.86603, 0.00574]};
            skSetInitialGuess(sketch, initialGuessF4);
            skSolve(sketch);
        }
        {
            var Q0;
            Q0 = qSketchRegion(id + "F3", true);
            extrude(context, id + "F5", {"entities" : qUnion([Q0]), "operationType" : NewBodyOperationType.REMOVE, "oppositeDirection" : true, "depth" : .6 * mm, "offsetDistance" : 25 * mm});
        }
        {
            var Q0;
            Q0 = qSketchRegion(id + "F4", true);
            var Q1;
            Q1 = qConstructionFilter(qBodyType(qCreatedBy(id + "F4" ,EDGE), BodyType.WIRE), ConstructionObject.NO);
            extrude(context, id + "F6", {"entities" : qUnion([Q0]), "operationType" : NewBodyOperationType.REMOVE, "surfaceEntities" : qUnion([Q1]), "oppositeDirection" : true, "depth" : .4 * mm, "offsetDistance" : 25 * mm});
        }
        {
            var Q0;
            Q0=makeQuery(id+"F5.boolean.opBoolean","COPY",EDGE,{"derivedFrom":makeQuery(id+"F5.opExtrude","CAP_EDGE",EDGE,{"disambiguationData":[OSD([sQuery(id+"F3.wireOp",EDGE,"E23.sketch_text.stroke-24")])],"isStart":true})});
            var Q1;
            Q1=makeQuery(id+"F5.boolean.opBoolean","COPY",EDGE,{"derivedFrom":makeQuery(id+"F5.opExtrude","CAP_EDGE",EDGE,{"disambiguationData":[OSD([sQuery(id+"F3.wireOp",EDGE,"E23.sketch_text.stroke-22")])],"isStart":true})});
            var Q2;
            Q2=makeQuery(id+"F5.boolean.opBoolean","COPY",EDGE,{"derivedFrom":makeQuery(id+"F5.opExtrude","CAP_EDGE",EDGE,{"disambiguationData":[OSD([sQuery(id+"F3.wireOp",EDGE,"E23.sketch_text.stroke-19")])],"isStart":true})});
            var Q3;
            Q3=makeQuery(id+"F5.boolean.opBoolean","COPY",EDGE,{"derivedFrom":makeQuery(id+"F5.opExtrude","CAP_EDGE",EDGE,{"disambiguationData":[OSD([sQuery(id+"F3.wireOp",EDGE,"E23.sketch_text.stroke-25")])],"isStart":true})});
            var Q4;
            Q4=makeQuery(id+"F5.boolean.opBoolean","COPY",EDGE,{"derivedFrom":makeQuery(id+"F5.opExtrude","CAP_EDGE",EDGE,{"disambiguationData":[OSD([sQuery(id+"F3.wireOp",EDGE,"E23.sketch_text.stroke-4")])],"isStart":true})});
            var Q5;
            Q5=makeQuery(id+"F5.boolean.opBoolean","COPY",EDGE,{"derivedFrom":makeQuery(id+"F5.opExtrude","CAP_EDGE",EDGE,{"disambiguationData":[OSD([sQuery(id+"F3.wireOp",EDGE,"E23.sketch_text.stroke-1")])],"isStart":true})});
            var Q6;
            Q6=makeQuery(id+"F5.boolean.opBoolean","COPY",EDGE,{"derivedFrom":makeQuery(id+"F5.opExtrude","CAP_EDGE",EDGE,{"disambiguationData":[OSD([sQuery(id+"F3.wireOp",EDGE,"E23.sketch_text.stroke-5")])],"isStart":true})});
            var Q7;
            Q7=makeQuery(id+"F5.boolean.opBoolean","COPY",EDGE,{"derivedFrom":makeQuery(id+"F5.opExtrude","CAP_EDGE",EDGE,{"disambiguationData":[OSD([sQuery(id+"F3.wireOp",EDGE,"E23.sketch_text.stroke-11")])],"isStart":true})});
            var Q8;
            Q8=makeQuery(id+"F5.boolean.opBoolean","COPY",EDGE,{"derivedFrom":makeQuery(id+"F5.opExtrude","CAP_EDGE",EDGE,{"disambiguationData":[OSD([sQuery(id+"F3.wireOp",EDGE,"E23.sketch_text.stroke-16")])],"isStart":true})});
            var Q9;
            Q9=makeQuery(id+"F5.boolean.opBoolean","COPY",EDGE,{"derivedFrom":makeQuery(id+"F5.opExtrude","CAP_EDGE",EDGE,{"disambiguationData":[OSD([sQuery(id+"F3.wireOp",EDGE,"E23.sketch_text.stroke-21")])],"isStart":true})});
            var Q10;
            Q10=makeQuery(id+"F5.boolean.opBoolean","COPY",EDGE,{"derivedFrom":makeQuery(id+"F5.opExtrude","CAP_EDGE",EDGE,{"disambiguationData":[OSD([sQuery(id+"F3.wireOp",EDGE,"E23.sketch_text.stroke-17")])],"isStart":true})});
            var Q11;
            Q11=makeQuery(id+"F5.boolean.opBoolean","COPY",EDGE,{"derivedFrom":makeQuery(id+"F5.opExtrude","CAP_EDGE",EDGE,{"disambiguationData":[OSD([sQuery(id+"F3.wireOp",EDGE,"E23.sketch_text.stroke-15")])],"isStart":true})});
            var Q12;
            Q12=makeQuery(id+"F5.boolean.opBoolean","COPY",EDGE,{"derivedFrom":makeQuery(id+"F5.opExtrude","CAP_EDGE",EDGE,{"disambiguationData":[OSD([sQuery(id+"F3.wireOp",EDGE,"E23.sketch_text.stroke-6")])],"isStart":false})});
            chamfer(context, id + "F7", {"entities" : qUnion([Q0, Q1, Q2, Q3, Q4, Q5, Q6, Q7, Q8, Q9, Q10, Q11, Q12]), "width" : .3 * mm, "tangentPropagation" : true});
        }
    });
